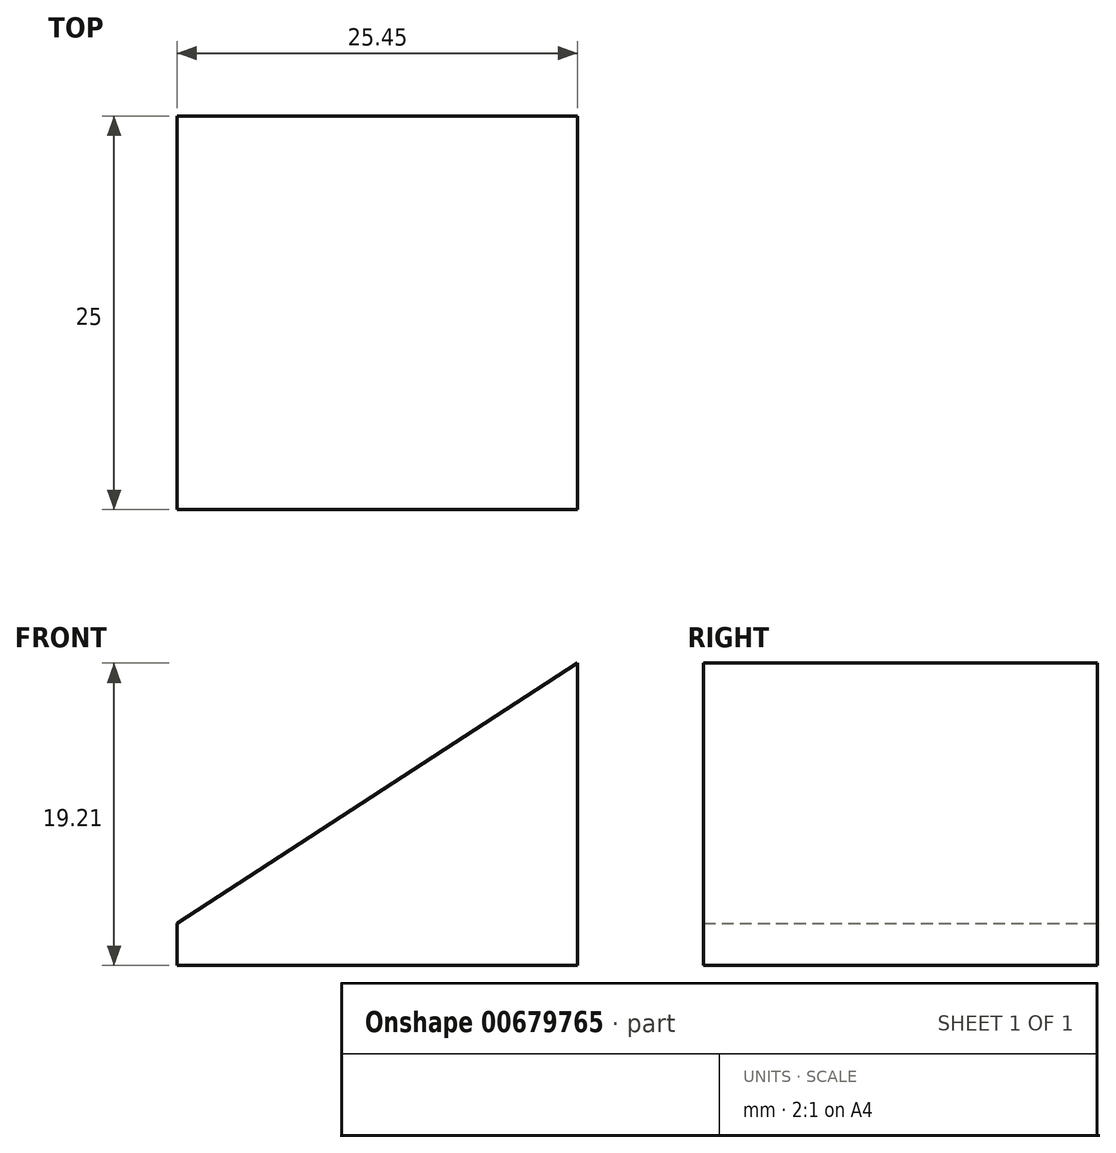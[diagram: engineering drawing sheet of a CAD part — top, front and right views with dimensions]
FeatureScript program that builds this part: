
annotation { "Feature Type Name" : "Feature", "Feature Type Description" : "" }
export const myFeature = defineFeature(function(context is Context, id is Id, definition is map)
    precondition{}
    {
        {
            var Q0;
            Q0=qCreatedBy(makeId("Front.planeOp"),FACE);
            var sketch = newSketch(context, id + "F0", { "sketchPlane" : qUnion([Q0])});
            skLineSegment(sketch, "E0", {"start": v(-25.45, 5.5) * mm, "end": v(-25.45, 2.82) * mm});
            skLineSegment(sketch, "E1", {"start": v(-25.45, 5.5) * mm, "end": v(0, 22.03) * mm});
            skLineSegment(sketch, "E2", {"start": v(0, 22.03) * mm, "end": v(0, 2.82) * mm});
            skLineSegment(sketch, "E3", {"start": v(0, 2.82) * mm, "end": v(-25.45, 2.82) * mm});
            skSolve(sketch);
        }
        {
            var Q0;
            Q0=makeQuery(id+"F0.imprint","IMPRINT",FACE,{"disambiguationData":[TD([[makeQuery(id+"F0.imprint","IMPRINT",EDGE,{"derivedFrom":sQuery(id+"F0.wireOp",EDGE,"E0")}),1.0]])]});
            extrude(context, id + "F1", {"entities" : qUnion([Q0]), "depth" : 25 * mm, "offsetDistance" : 25 * mm});
        }
    });
